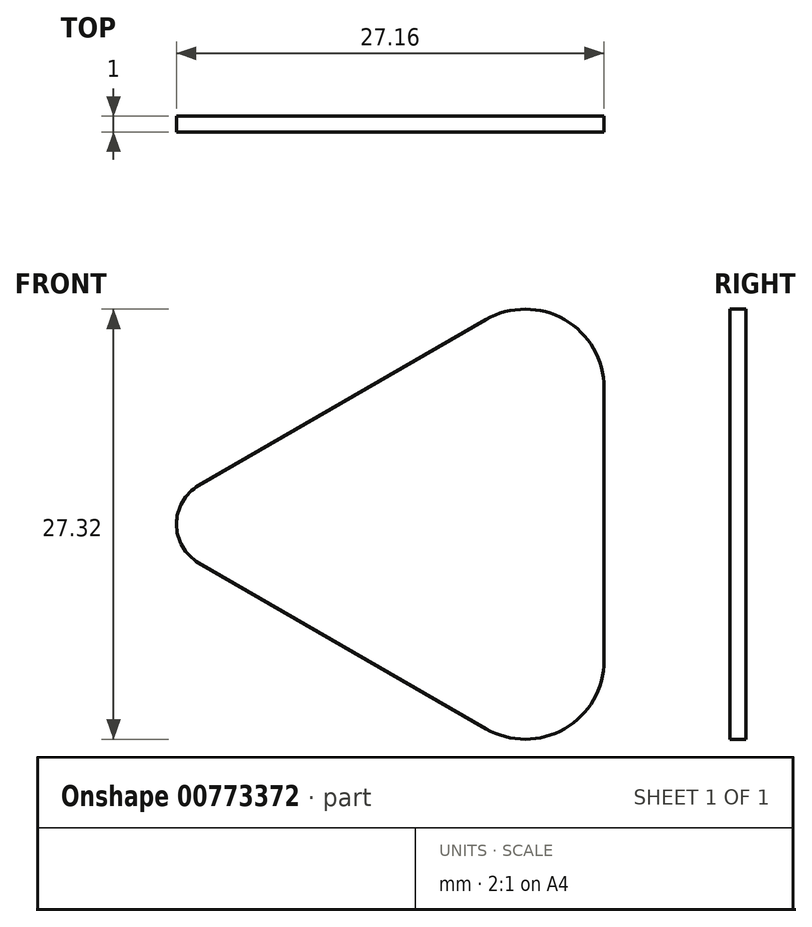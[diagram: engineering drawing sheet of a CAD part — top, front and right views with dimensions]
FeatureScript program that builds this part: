
annotation { "Feature Type Name" : "Feature", "Feature Type Description" : "" }
export const myFeature = defineFeature(function(context is Context, id is Id, definition is map)
    precondition{}
    {
        {
            var Q0;
            Q0=qCreatedBy(makeId("Front.planeOp"),FACE);
            var sketch = newSketch(context, id + "F0", { "sketchPlane" : qUnion([Q0])});
            skCircle(sketch, "E0.cCircle", {"center": v(0, 0) * mm, "radius": 10 * mm, "construction": true});
            skLineSegment(sketch, "E0.0", {"start": v(10, 8.66) * mm, "end": v(10, -8.66) * mm});
            skLineSegment(sketch, "E0.1", {"start": v(2.5, -13) * mm, "end": v(-15.74, -2.46) * mm});
            skLineSegment(sketch, "E0.2", {"start": v(-15.74, 2.46) * mm, "end": v(2.5, 13) * mm});
            skPoint(sketch, "E0.0.midPoint", {"position": v(10, 0) * mm});
            skPoint(sketch, "E1.visualSharp", {"position": v(10, 17.32) * mm});
            skArc(sketch, "E1.filletArc", {"start": v(10, 16.97) * mm, "mid": v(9.9, 17.15) * mm, "end": v(9.7, 17.15) * mm});
            skArc(sketch, "E2.filletArc", {"start": v(10, 13.86) * mm, "mid": v(9, 15.59) * mm, "end": v(7, 15.59) * mm});
            skPoint(sketch, "E3.visualSharp", {"position": v(10, -17.32) * mm});
            skArc(sketch, "E3.filletArc", {"start": v(2.5, -13) * mm, "mid": v(7.5, -13) * mm, "end": v(10, -8.66) * mm});
            skArc(sketch, "E4.filletArc", {"start": v(10, 8.66) * mm, "mid": v(7.5, 13) * mm, "end": v(2.5, 13) * mm});
            skPoint(sketch, "E5.visualSharp", {"position": v(-20, 0) * mm});
            skArc(sketch, "E5.filletArc", {"start": v(-15.74, 2.46) * mm, "mid": v(-17.16, 0) * mm, "end": v(-15.74, -2.46) * mm});
            skSolve(sketch);
        }
        {
            var Q0;
            Q0=makeQuery(id+"F0.imprint","IMPRINT",FACE,{"disambiguationData":[TD([[makeQuery(id+"F0.imprint","IMPRINT",EDGE,{"derivedFrom":sQuery(id+"F0.wireOp",EDGE,"E0.0")}),-1.0]])]});
            extrude(context, id + "F1", {"entities" : qUnion([Q0]), "depth" : 1 * mm, "offsetDistance" : 25 * mm});
        }
    });
